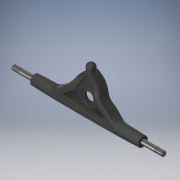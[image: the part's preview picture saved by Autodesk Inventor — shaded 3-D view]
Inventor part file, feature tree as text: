
AUTODESK INVENTOR PART (.ipt)
format: ipt  version: 2019 (Build 230136000, 136)  size: 9,888,256 bytes
history: native  units: mm
features: other x14, sketch x13, fillet x12, extrude x12, plane x3, thicken_offset x3, chamfer x2, thread x2, revolve x1, surface_op x1
ambient origin geometry x8: Origin, YZ Plane, XZ Plane, XY Plane, X Axis, Y Axis, Z Axis, Center Point
bodies: Body1 (feature_tree), Body2 (feature_tree), Body3 (feature_tree), Body4 (feature_tree)
feature tree (63):
  revolve  "Revolution1"  [1 undecoded]
  fillet  "Fillet2"  Radius=8.0mm
  extrude  "Extrusion2"  Depth=9.4mm
  extrude  "Extrusion3"  Depth=9.4mm
  sketch  "Sketch1"  dims[d87=102.0mm d156=90.5mm d181=8.0mm]
  plane  "Work Plane1"
  sketch  "Sketch6"  dims[d191=90.0deg d193=1.0mm]
  sketch  "3D Sketch4"
  thicken_offset  "Thicken18"
  sketch  "Sketch8"  dims[d194=8.0mm d195=35.0mm d196=0.0mm]
  extrude  "Extrusion10"  Depth=8.0mm
  sketch  "Sketch9"  dims[d197=8.0mm d198=35.0mm d199=0.0mm d207=0.0mm d261=15.0mm]
  extrude  "Extrusion11"  Depth=1.0mm
  extrude  "Extrusion12"  Depth=35.0mm TaperAngle=0.0deg
  extrude  "Extrusion15"  Depth=35.0mm TaperAngle=0.0deg
  fillet  "Fillet10"  [1 undecoded]
  fillet  "Fillet11"  Radius=15.0mm
  extrude  "Extrusion14"  Depth=15.0mm
  extrude  "Extrusion16"  TaperAngle=0.0deg  [1 undecoded]
  fillet  "Fillet15"  Radius=18.0mm
  fillet  "Fillet17"  Radius=18.0mm
  fillet  "Fillet18"  Radius=10.0mm
  fillet  "Fillet19"  Radius=2.0mm
  fillet  "Fillet20"  Radius=33.0mm
  fillet  "Fillet21"  Radius=2.0mm
  chamfer  "Chamfer1"  Distance=10.0mm
  extrude  "Extrusion19"  Depth=5.0mm
  extrude  "Extrusion20"  Depth=1.0mm
  chamfer  "Chamfer2"  Distance=2.0mm
  thread  "Thread1"  [1 undecoded]
  thread  "Thread2"  [1 undecoded]
  fillet  "Fillet22"  Radius=1.0mm
  fillet  "Fillet23"  Radius=1.0mm
  fillet  "Fillet25"  Radius=1.0mm
  other  "Form13"
  thicken_offset  "Thicken21"
  thicken_offset  "Thicken22"
  plane  "Work Plane3"
  extrude  "Extrusion21"  Depth=1.0mm
  plane  "Work Plane5"
  extrude  "Extrusion22"  Depth=0.5mm TaperAngle=45.0deg
  other  "Image1"
  sketch  "Sketch2"  dims[d185=9.0mm d186=9.4mm]
  other  "Image3"
  sketch  "Sketch3"  dims[d187=9.5mm d188=9.4mm]
  sketch  "Sketch4"  dims[d189=9.0mm d190=8.0mm]
  other  "Image5"
  other  "Image6"
  other  "3D Intersection4"
  other  "Srf30"
  sketch  "Sketch13"  dims[d374=30.0mm d539=15.0mm]
  sketch  "Sketch14"  dims[d540=24.0mm d546=0.0mm d547=18.0mm d548=18.0mm d549=10.0mm d550=0.0mm]
  sketch  "Sketch15"  dims[d551=4.0mm d552=6.0mm d553=0.0mm d554=0.0mm d571=2.0mm d572=0.0mm d573=33.0mm d578=2.0mm d579=0.0mm]
  other  "Matched Edge29"
  other  "Matches"
  other  "Matched Edge30"
  other  "Matched Edge31"
  other  "Matched Edge32"
  sketch  "Sketch16"  dims[d581=7.5mm]
  sketch  "Sketch18"  dims[d582=13.0mm d583=10.0mm d584=3.0mm d585=0.0mm d586=0.0mm d587=5.0mm d588=1.0mm d592=2.0mm d593=6.0mm d594=0.0mm d595=0.0mm d596=1.0mm d598=1.0mm d599=1.0mm d600=1.0mm d601=1.0mm d602=1.0mm d603=0.5mm d604=2.0mm d605=45.0deg d608=0.1mm d611=12.0mm d612=0.0mm d613=12.0mm d614=0.0mm d615=0.5mm d616=2.0mm d617=45.0deg d618=10.0mm d619=0.0mm d620=10.0mm d621=0.0mm d622=3.0mm d623=1.0mm d624=2.0mm d626=2.0mm d639=0.001mm d640=10.0mm d641=0.001mm d642=10.0mm d643=0.001mm d644=10.0mm d645=0.001mm d646=10.0mm d647=5.0mm d648=5.0mm d649=5.0mm d650=5.0mm d651=12.0mm d652=0.0mm d653=10.0mm d655=0.0mm d656=0.0mm]
  surface_op  "Boundary Patch5"
  other  "Srf37"
  other  "Srf39"
note: 5 required parameter values undecoded (feature->parameter linkage not recoverable at this tier; creation-order binding heuristic only, values carry confidence <= 0.55)